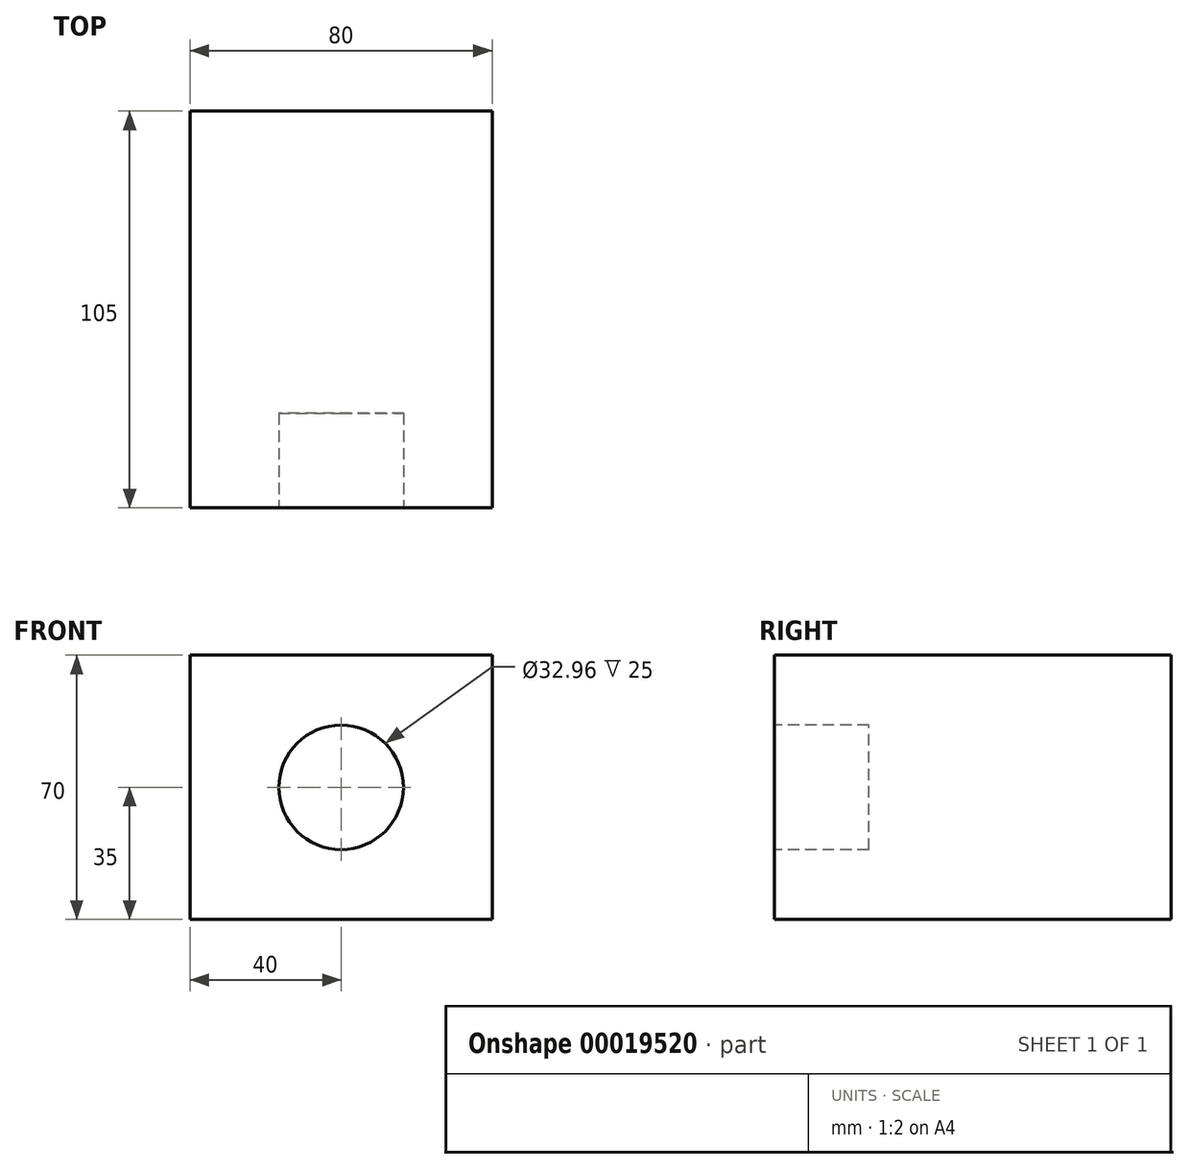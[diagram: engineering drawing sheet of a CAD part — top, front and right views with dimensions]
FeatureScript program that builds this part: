
annotation { "Feature Type Name" : "Feature", "Feature Type Description" : "" }
export const myFeature = defineFeature(function(context is Context, id is Id, definition is map)
    precondition{}
    {
        {
            var Q0;
            Q0=qCreatedBy(makeId("Front.planeOp"),FACE);
            var sketch = newSketch(context, id + "F0", { "sketchPlane" : qUnion([Q0])});
            skLineSegment(sketch, "E0.rect.bottom", {"start": v(-40, -35) * mm, "end": v(40, -35) * mm});
            skLineSegment(sketch, "E0.rect.top", {"start": v(-40, 35) * mm, "end": v(40, 35) * mm});
            skLineSegment(sketch, "E0.rect.left", {"start": v(-40, -35) * mm, "end": v(-40, 35) * mm});
            skLineSegment(sketch, "E0.rect.right", {"start": v(40, -35) * mm, "end": v(40, 35) * mm});
            skPoint(sketch, "E0.rect.middle", {"position": v(0, 0) * mm});
            skSolve(sketch);
        }
        {
            var Q0;
            Q0=makeQuery(id+"F0.imprint","IMPRINT",FACE,{"disambiguationData":[TD([[makeQuery(id+"F0.imprint","IMPRINT",EDGE,{"derivedFrom":sQuery(id+"F0.wireOp",EDGE,"E0.rect.bottom")}),1.0]])]});
            extrude(context, id + "F1", {"entities" : qUnion([Q0]), "endBound" : BoundingType.SYMMETRIC, "oppositeDirection" : true, "depth" : 105 * mm});
        }
        {
            var Q0;
            Q0=makeQuery(id+"F1.opExtrude","CAP_FACE",FACE,{"disambiguationData":[OSD([sQuery(id+"F0.wireOp",EDGE,"E0.rect.bottom"),sQuery(id+"F0.wireOp",EDGE,"E0.rect.top"),sQuery(id+"F0.wireOp",EDGE,"E0.rect.left"),sQuery(id+"F0.wireOp",EDGE,"E0.rect.right")])],"isStart":true});
            var sketch = newSketch(context, id + "F2", { "sketchPlane" : qUnion([Q0])});
            skCircle(sketch, "E1", {"center": v(0, 0) * mm, "radius": 16.48 * mm});
            skSolve(sketch);
        }
        {
            var Q0;
            Q0=makeQuery(id+"F2.imprint","IMPRINT",FACE,{"disambiguationData":[TD([[makeQuery(id+"F2.imprint","IMPRINT",EDGE,{"derivedFrom":sQuery(id+"F2.wireOp",EDGE,"E1")}),1.0]])]});
            extrude(context, id + "F3", {"entities" : qUnion([Q0]), "operationType" : NewBodyOperationType.REMOVE, "oppositeDirection" : true, "depth" : 25 * mm});
        }
    });
